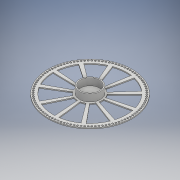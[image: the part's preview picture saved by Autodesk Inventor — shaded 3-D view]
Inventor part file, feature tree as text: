
AUTODESK INVENTOR PART (.ipt)
format: ipt  version: 2017 (Build 210142000, 142)  size: 339,456 bytes
history: native  units: mm
features: extrude x2, sketch x2
ambient origin geometry x8: Origin, YZ Plane, XZ Plane, XY Plane, X Axis, Y Axis, Z Axis, Center Point
bodies: Solid1 (feature_tree)
feature tree (4):
  extrude  "Extrusion1"  Depth=115.0mm
  extrude  "Extrusion2"  Depth=105.0mm TaperAngle=360.0deg
  sketch  "Sketch1"  dims[d0=240.0mm d1=115.0mm]
  sketch  "Sketch2"  dims[d2=5.0mm d3=1000.0mm d5=360.0deg d7=3.0mm d8=0.0mm d9=54.0mm d10=60.0mm d11=20.0mm d12=0.0mm d13=105.0mm d14=30.0deg d15=95.0mm d16=95.0mm d17=15.0deg d18=95.0mm d19=15.0deg d20=105.0mm d21=110.0mm d23=360.0deg d25=70.0mm]
